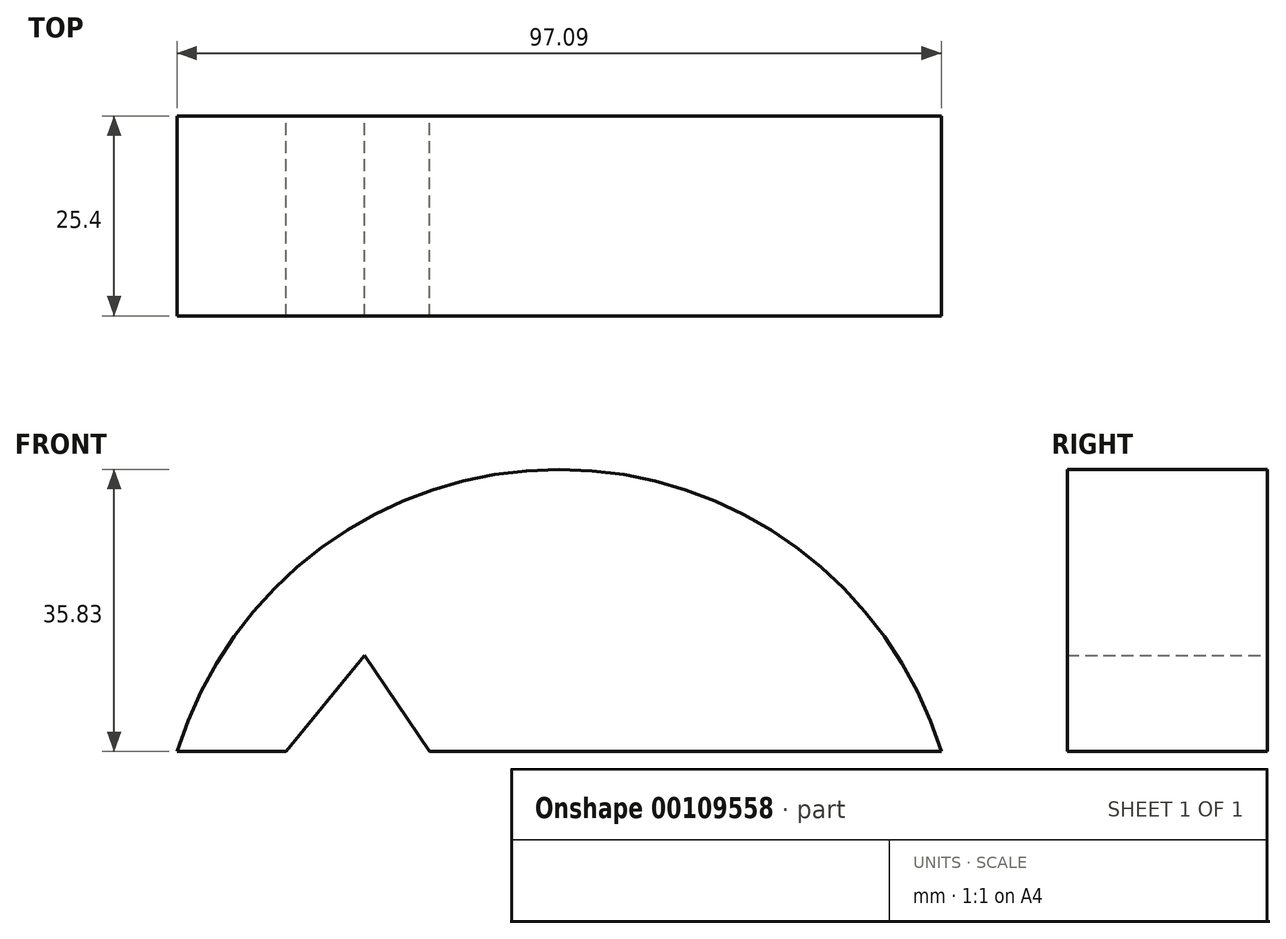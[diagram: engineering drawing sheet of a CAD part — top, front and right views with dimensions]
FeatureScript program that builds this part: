
annotation { "Feature Type Name" : "Feature", "Feature Type Description" : "" }
export const myFeature = defineFeature(function(context is Context, id is Id, definition is map)
    precondition{}
    {
        {
            var Q0;
            Q0=qCreatedBy(makeId("Front.planeOp"),FACE);
            var sketch = newSketch(context, id + "F0", { "sketchPlane" : qUnion([Q0])});
            skLineSegment(sketch, "E0", {"start": v(-57.55, 28.46) * mm, "end": v(39.54, 28.46) * mm});
            skArc(sketch, "E1", {"start": v(39.54, 28.46) * mm, "mid": v(-9, 64.29) * mm, "end": v(-57.55, 28.46) * mm});
            skLineSegment(sketch, "E2", {"start": v(-43.68, 28.46) * mm, "end": v(-33.74, 40.68) * mm});
            skLineSegment(sketch, "E3", {"start": v(-33.74, 40.68) * mm, "end": v(-25.46, 28.46) * mm});
            skLineSegment(sketch, "E4", {"start": v(-25.46, 28.46) * mm, "end": v(-43.68, 28.46) * mm});
            skSolve(sketch);
        }
        {
            var Q0;
            {var subQ1=sQuery(id+"F0.wireOp",EDGE,"E1");Q0=makeQuery(id+"F0.imprint","IMPRINT",FACE,{"disambiguationData":[TD([[makeQuery(id+"F0.imprint","IMPRINT",EDGE,{"derivedFrom":subQ1}),1.0]])]});}
            extrude(context, id + "F1", {"entities" : qUnion([Q0]), "depth" : 25.4 * mm});
        }
    });
